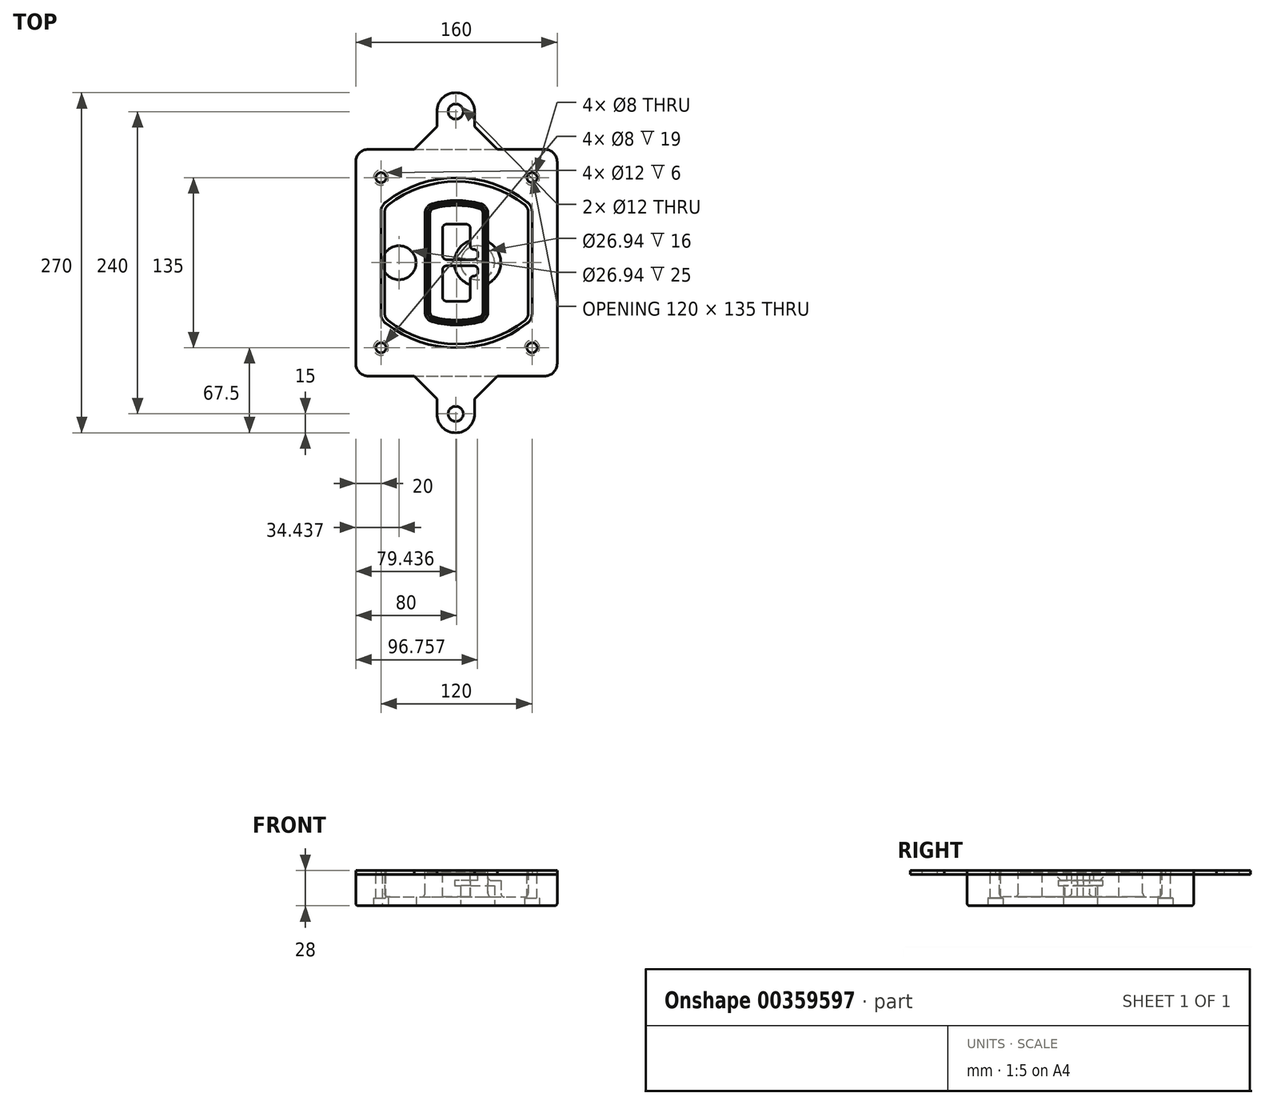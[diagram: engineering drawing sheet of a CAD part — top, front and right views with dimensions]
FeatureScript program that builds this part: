
annotation { "Feature Type Name" : "Feature", "Feature Type Description" : "" }
export const myFeature = defineFeature(function(context is Context, id is Id, definition is map)
    precondition{}
    {
        {
            var Q0;
            Q0=qCreatedBy(makeId("Top.planeOp"),FACE);
            var sketch = newSketch(context, id + "F0", { "sketchPlane" : qUnion([Q0])});
            skPoint(sketch, "E0.rect.middle", {"position": v(0, 0) * mm});
            skLineSegment(sketch, "E1.bottom", {"start": v(-70, -90) * mm, "end": v(70, -90) * mm});
            skLineSegment(sketch, "E1.top", {"start": v(-70, 90) * mm, "end": v(70, 90) * mm});
            skLineSegment(sketch, "E1.left", {"start": v(-80, -80) * mm, "end": v(-80, 80) * mm});
            skLineSegment(sketch, "E1.right", {"start": v(80, -80) * mm, "end": v(80, 80) * mm});
            skLineSegment(sketch, "E2", {"start": v(-80, 90) * mm, "end": v(80, -90) * mm, "construction": true});
            skLineSegment(sketch, "E3", {"start": v(80, 90) * mm, "end": v(-80, -90) * mm, "construction": true});
            skCircle(sketch, "E4", {"center": v(-60, 67.5) * mm, "radius": 4 * mm});
            skCircle(sketch, "E5", {"center": v(60, 67.5) * mm, "radius": 4 * mm});
            skCircle(sketch, "E6", {"center": v(60, -67.5) * mm, "radius": 4 * mm});
            skCircle(sketch, "E7", {"center": v(-60, -67.5) * mm, "radius": 4 * mm});
            skLineSegment(sketch, "E8", {"start": v(-60, 67.5) * mm, "end": v(60, 67.5) * mm, "construction": true});
            skLineSegment(sketch, "E9", {"start": v(60, 67.5) * mm, "end": v(60, -67.5) * mm, "construction": true});
            skLineSegment(sketch, "E10", {"start": v(60, -67.5) * mm, "end": v(-60, -67.5) * mm, "construction": true});
            skLineSegment(sketch, "E11", {"start": v(-60, -67.5) * mm, "end": v(-60, 67.5) * mm, "construction": true});
            skLineSegment(sketch, "E12", {"start": v(-60, 40.3) * mm, "end": v(-60, -40.3) * mm});
            skLineSegment(sketch, "E13", {"start": v(60, 40.3) * mm, "end": v(60, -40.3) * mm});
            skArc(sketch, "E14", {"start": v(56.15, 48.18) * mm, "mid": v(0, 67.5) * mm, "end": v(-56.15, 48.18) * mm});
            skArc(sketch, "E15", {"start": v(-56.15, -48.18) * mm, "mid": v(0, -67.5) * mm, "end": v(56.15, -48.18) * mm});
            skLineSegment(sketch, "E16", {"start": v(-60, 0) * mm, "end": v(60, 0) * mm, "construction": true});
            skPoint(sketch, "E17.visualSharp", {"position": v(-60, -45) * mm});
            skArc(sketch, "E17.filletArc", {"start": v(-60, -40.3) * mm, "mid": v(-58.99, -44.68) * mm, "end": v(-56.15, -48.18) * mm});
            skPoint(sketch, "E18.visualSharp", {"position": v(-60, 45) * mm});
            skArc(sketch, "E18.filletArc", {"start": v(-56.15, 48.18) * mm, "mid": v(-58.99, 44.68) * mm, "end": v(-60, 40.3) * mm});
            skPoint(sketch, "E19.visualSharp", {"position": v(60, 45) * mm});
            skArc(sketch, "E19.filletArc", {"start": v(60, 40.3) * mm, "mid": v(58.99, 44.68) * mm, "end": v(56.15, 48.18) * mm});
            skPoint(sketch, "E20.visualSharp", {"position": v(60, -45) * mm});
            skArc(sketch, "E20.filletArc", {"start": v(56.15, -48.18) * mm, "mid": v(58.99, -44.68) * mm, "end": v(60, -40.3) * mm});
            skPoint(sketch, "E21.visualSharp", {"position": v(-80, 90) * mm});
            skArc(sketch, "E21.filletArc", {"start": v(-70, 90) * mm, "mid": v(-77.07, 87.07) * mm, "end": v(-80, 80) * mm});
            skPoint(sketch, "E22.visualSharp", {"position": v(80, 90) * mm});
            skArc(sketch, "E22.filletArc", {"start": v(80, 80) * mm, "mid": v(77.07, 87.07) * mm, "end": v(70, 90) * mm});
            skPoint(sketch, "E23.visualSharp", {"position": v(80, -90) * mm});
            skArc(sketch, "E23.filletArc", {"start": v(70, -90) * mm, "mid": v(77.07, -87.07) * mm, "end": v(80, -80) * mm});
            skPoint(sketch, "E24.visualSharp", {"position": v(-80, -90) * mm});
            skArc(sketch, "E24.filletArc", {"start": v(-80, -80) * mm, "mid": v(-77.07, -87.07) * mm, "end": v(-70, -90) * mm});
            skArc(sketch, "E25.0", {"start": v(57, 40.3) * mm, "mid": v(56.3, 43.36) * mm, "end": v(54.3, 45.81) * mm});
            skLineSegment(sketch, "E25.1", {"start": v(57, 40.3) * mm, "end": v(57, -40.3) * mm});
            skArc(sketch, "E25.2", {"start": v(54.3, -45.81) * mm, "mid": v(56.3, -43.36) * mm, "end": v(57, -40.3) * mm});
            skArc(sketch, "E25.3", {"start": v(-54.3, -45.81) * mm, "mid": v(0, -64.5) * mm, "end": v(54.3, -45.81) * mm});
            skArc(sketch, "E25.4", {"start": v(-57, -40.3) * mm, "mid": v(-56.3, -43.36) * mm, "end": v(-54.3, -45.81) * mm});
            skArc(sketch, "E25.5", {"start": v(54.3, 45.81) * mm, "mid": v(0, 64.5) * mm, "end": v(-54.3, 45.81) * mm});
            skLineSegment(sketch, "E25.6", {"start": v(-57, 40.3) * mm, "end": v(-57, -40.3) * mm});
            skArc(sketch, "E25.7", {"start": v(-54.3, 45.81) * mm, "mid": v(-56.3, 43.36) * mm, "end": v(-57, 40.3) * mm});
            skArc(sketch, "E26.0", {"start": v(-58.62, 51.33) * mm, "mid": v(-62.58, 46.43) * mm, "end": v(-64, 40.3) * mm});
            skArc(sketch, "E26.1", {"start": v(58.62, 51.33) * mm, "mid": v(0, 71.5) * mm, "end": v(-58.62, 51.33) * mm});
            skArc(sketch, "E26.2", {"start": v(64, 40.3) * mm, "mid": v(62.58, 46.43) * mm, "end": v(58.62, 51.33) * mm});
            skLineSegment(sketch, "E26.3", {"start": v(64, 40.3) * mm, "end": v(64, -40.3) * mm});
            skArc(sketch, "E26.4", {"start": v(58.62, -51.33) * mm, "mid": v(62.58, -46.43) * mm, "end": v(64, -40.3) * mm});
            skLineSegment(sketch, "E26.5", {"start": v(-64, 40.3) * mm, "end": v(-64, -40.3) * mm});
            skArc(sketch, "E26.6", {"start": v(-58.62, -51.33) * mm, "mid": v(0, -71.5) * mm, "end": v(58.62, -51.33) * mm});
            skArc(sketch, "E26.7", {"start": v(-64, -40.3) * mm, "mid": v(-62.58, -46.43) * mm, "end": v(-58.62, -51.33) * mm});
            skSolve(sketch);
        }
        {
            var Q0;
            Q0=makeQuery(id+"F0.imprint","IMPRINT",FACE,{"disambiguationData":[TD([[makeQuery(id+"F0.imprint","IMPRINT",EDGE,{"derivedFrom":sQuery(id+"F0.wireOp",EDGE,"E1.bottom")}),1.0]])]});
            var Q1;
            Q1=makeQuery(id+"F0.imprint","IMPRINT",FACE,{"disambiguationData":[TD([[makeQuery(id+"F0.imprint","IMPRINT",EDGE,{"derivedFrom":sQuery(id+"F0.wireOp",EDGE,"E12")}),1.0]])]});
            var Q2;
            Q2=makeQuery(id+"F0.imprint","IMPRINT",FACE,{"disambiguationData":[TD([[makeQuery(id+"F0.imprint","IMPRINT",EDGE,{"derivedFrom":sQuery(id+"F0.wireOp",EDGE,"E25.0")}),1.0]])]});
            var Q3;
            Q3=makeQuery(id+"F0.imprint","IMPRINT",FACE,{"disambiguationData":[TD([[makeQuery(id+"F0.imprint","IMPRINT",EDGE,{"derivedFrom":sQuery(id+"F0.wireOp",EDGE,"E12")}),-1.0]])]});
            extrude(context, id + "F1", {"entities" : qUnion([Q0, Q1, Q2, Q3]), "oppositeDirection" : true, "depth" : 25 * mm});
        }
        {
            var Q0;
            Q0=makeQuery(id+"F0.imprint","IMPRINT",FACE,{"disambiguationData":[TD([[makeQuery(id+"F0.imprint","IMPRINT",EDGE,{"derivedFrom":sQuery(id+"F0.wireOp",EDGE,"E12")}),1.0]])]});
            extrude(context, id + "F2", {"entities" : qUnion([Q0]), "operationType" : NewBodyOperationType.ADD, "depth" : 3 * mm});
        }
        {
            var Q0;
            Q0=makeQuery(id+"F0.imprint","IMPRINT",FACE,{"disambiguationData":[TD([[makeQuery(id+"F0.imprint","IMPRINT",EDGE,{"derivedFrom":sQuery(id+"F0.wireOp",EDGE,"E25.0")}),1.0]])]});
            extrude(context, id + "F3", {"entities" : qUnion([Q0]), "operationType" : NewBodyOperationType.REMOVE, "oppositeDirection" : true, "depth" : 18 * mm});
        }
        {
            var Q0;
            Q0=makeQuery(id+"F2.opExtrude","CAP_FACE",FACE,{"disambiguationData":[OSD([sQuery(id+"F0.wireOp",EDGE,"E12"),sQuery(id+"F0.wireOp",EDGE,"E13"),sQuery(id+"F0.wireOp",EDGE,"E14"),sQuery(id+"F0.wireOp",EDGE,"E15"),sQuery(id+"F0.wireOp",EDGE,"E17.filletArc"),sQuery(id+"F0.wireOp",EDGE,"E18.filletArc"),sQuery(id+"F0.wireOp",EDGE,"E19.filletArc"),sQuery(id+"F0.wireOp",EDGE,"E20.filletArc"),sQuery(id+"F0.wireOp",EDGE,"E25.0"),sQuery(id+"F0.wireOp",EDGE,"E25.1"),sQuery(id+"F0.wireOp",EDGE,"E25.2"),sQuery(id+"F0.wireOp",EDGE,"E25.3"),sQuery(id+"F0.wireOp",EDGE,"E25.4"),sQuery(id+"F0.wireOp",EDGE,"E25.5"),sQuery(id+"F0.wireOp",EDGE,"E25.6"),sQuery(id+"F0.wireOp",EDGE,"E25.7")])],"isStart":false});
            var sketch = newSketch(context, id + "F4", { "sketchPlane" : qUnion([Q0])});
            skArc(sketch, "E27.0", {"start": v(-19.08, -46.97) * mm, "mid": v(0, -49.5) * mm, "end": v(19.08, -46.97) * mm});
            skArc(sketch, "E28.0", {"start": v(19.08, 46.97) * mm, "mid": v(0, 49.5) * mm, "end": v(-19.08, 46.97) * mm});
            skLineSegment(sketch, "E29", {"start": v(-25, 39.25) * mm, "end": v(-25, -39.25) * mm});
            skLineSegment(sketch, "E30", {"start": v(25, 39.25) * mm, "end": v(25, -39.25) * mm});
            skLineSegment(sketch, "E31", {"start": v(-25, 45.1) * mm, "end": v(25, 45.1) * mm, "construction": true});
            skLineSegment(sketch, "E32", {"start": v(-25, -45.1) * mm, "end": v(25, -45.1) * mm, "construction": true});
            skPoint(sketch, "E33.visualSharp", {"position": v(-25, 45.1) * mm});
            skArc(sketch, "E33.filletArc", {"start": v(-19.08, 46.97) * mm, "mid": v(-23.35, 44.11) * mm, "end": v(-25, 39.25) * mm});
            skPoint(sketch, "E34.visualSharp", {"position": v(25, 45.1) * mm});
            skArc(sketch, "E34.filletArc", {"start": v(25, 39.25) * mm, "mid": v(23.35, 44.11) * mm, "end": v(19.08, 46.97) * mm});
            skPoint(sketch, "E35.visualSharp", {"position": v(25, -45.1) * mm});
            skArc(sketch, "E35.filletArc", {"start": v(19.08, -46.97) * mm, "mid": v(23.35, -44.11) * mm, "end": v(25, -39.25) * mm});
            skPoint(sketch, "E36.visualSharp", {"position": v(-25, -45.1) * mm});
            skArc(sketch, "E36.filletArc", {"start": v(-25, -39.25) * mm, "mid": v(-23.35, -44.11) * mm, "end": v(-19.08, -46.97) * mm});
            skArc(sketch, "E37.0", {"start": v(54.3, 45.81) * mm, "mid": v(0, 64.5) * mm, "end": v(-54.3, 45.81) * mm});
            skArc(sketch, "E37.1", {"start": v(-54.3, 45.81) * mm, "mid": v(-56.3, 43.36) * mm, "end": v(-57, 40.3) * mm});
            skLineSegment(sketch, "E37.2", {"start": v(-57, 40.3) * mm, "end": v(-57, -40.3) * mm});
            skArc(sketch, "E37.3", {"start": v(-57, -40.3) * mm, "mid": v(-56.3, -43.36) * mm, "end": v(-54.3, -45.81) * mm});
            skArc(sketch, "E37.4", {"start": v(-54.3, -45.81) * mm, "mid": v(0, -64.5) * mm, "end": v(54.3, -45.81) * mm});
            skArc(sketch, "E37.5", {"start": v(54.3, -45.81) * mm, "mid": v(56.3, -43.36) * mm, "end": v(57, -40.3) * mm});
            skLineSegment(sketch, "E37.6", {"start": v(57, 40.3) * mm, "end": v(57, -40.3) * mm});
            skArc(sketch, "E37.7", {"start": v(57, 40.3) * mm, "mid": v(56.3, 43.36) * mm, "end": v(54.3, 45.81) * mm});
            skLineSegment(sketch, "E38.0", {"start": v(23, 39.25) * mm, "end": v(23, -39.25) * mm});
            skArc(sketch, "E38.1", {"start": v(18.56, -45.04) * mm, "mid": v(21.76, -42.9) * mm, "end": v(23, -39.25) * mm});
            skArc(sketch, "E38.2", {"start": v(-18.56, -45.04) * mm, "mid": v(0, -47.5) * mm, "end": v(18.56, -45.04) * mm});
            skArc(sketch, "E38.3", {"start": v(-23, -39.25) * mm, "mid": v(-21.76, -42.9) * mm, "end": v(-18.56, -45.04) * mm});
            skLineSegment(sketch, "E38.4", {"start": v(-23, 39.25) * mm, "end": v(-23, -39.25) * mm});
            skArc(sketch, "E38.5", {"start": v(23, 39.25) * mm, "mid": v(21.76, 42.9) * mm, "end": v(18.56, 45.04) * mm});
            skArc(sketch, "E38.6", {"start": v(-18.56, 45.04) * mm, "mid": v(-21.76, 42.9) * mm, "end": v(-23, 39.25) * mm});
            skArc(sketch, "E38.7", {"start": v(18.56, 45.04) * mm, "mid": v(0, 47.5) * mm, "end": v(-18.56, 45.04) * mm});
            skArc(sketch, "E39.0", {"start": v(21, 39.25) * mm, "mid": v(20.18, 41.68) * mm, "end": v(18.04, 43.1) * mm});
            skLineSegment(sketch, "E39.1", {"start": v(21, 39.25) * mm, "end": v(21, -39.25) * mm});
            skArc(sketch, "E39.2", {"start": v(18.04, -43.1) * mm, "mid": v(20.18, -41.68) * mm, "end": v(21, -39.25) * mm});
            skArc(sketch, "E39.3", {"start": v(-18.04, -43.1) * mm, "mid": v(0, -45.5) * mm, "end": v(18.04, -43.1) * mm});
            skArc(sketch, "E39.4", {"start": v(-21, -39.25) * mm, "mid": v(-20.18, -41.68) * mm, "end": v(-18.04, -43.1) * mm});
            skArc(sketch, "E39.5", {"start": v(18.04, 43.1) * mm, "mid": v(0, 45.5) * mm, "end": v(-18.04, 43.1) * mm});
            skLineSegment(sketch, "E39.6", {"start": v(-21, 39.25) * mm, "end": v(-21, -39.25) * mm});
            skArc(sketch, "E39.7", {"start": v(-18.04, 43.1) * mm, "mid": v(-20.18, 41.68) * mm, "end": v(-21, 39.25) * mm});
            skLineSegment(sketch, "E40", {"start": v(-25, 0) * mm, "end": v(25, 0) * mm, "construction": true});
            skLineSegment(sketch, "E41", {"start": v(-11, 5.5) * mm, "end": v(-11, 27.5) * mm});
            skLineSegment(sketch, "E42", {"start": v(-8, 30.5) * mm, "end": v(8, 30.5) * mm});
            skLineSegment(sketch, "E43", {"start": v(11, 27.5) * mm, "end": v(11, 13.5) * mm});
            skLineSegment(sketch, "E44", {"start": v(14, 10.5) * mm, "end": v(14, 10.5) * mm});
            skLineSegment(sketch, "E45", {"start": v(17, 7.5) * mm, "end": v(17, 5.5) * mm});
            skLineSegment(sketch, "E46", {"start": v(14, 2.5) * mm, "end": v(-8, 2.5) * mm});
            skPoint(sketch, "E47.visualSharp", {"position": v(-11, 30.5) * mm});
            skArc(sketch, "E47.filletArc", {"start": v(-8, 30.5) * mm, "mid": v(-10.12, 29.62) * mm, "end": v(-11, 27.5) * mm});
            skPoint(sketch, "E48.visualSharp", {"position": v(11, 30.5) * mm});
            skArc(sketch, "E48.filletArc", {"start": v(11, 27.5) * mm, "mid": v(10.12, 29.62) * mm, "end": v(8, 30.5) * mm});
            skPoint(sketch, "E49.visualSharp", {"position": v(11, 10.5) * mm});
            skArc(sketch, "E49.filletArc", {"start": v(11, 13.5) * mm, "mid": v(11.88, 11.38) * mm, "end": v(14, 10.5) * mm});
            skPoint(sketch, "E50.visualSharp", {"position": v(17, 10.5) * mm});
            skArc(sketch, "E50.filletArc", {"start": v(17, 7.5) * mm, "mid": v(16.12, 9.62) * mm, "end": v(14, 10.5) * mm});
            skPoint(sketch, "E51.visualSharp", {"position": v(17, 2.5) * mm});
            skArc(sketch, "E51.filletArc", {"start": v(14, 2.5) * mm, "mid": v(16.12, 3.38) * mm, "end": v(17, 5.5) * mm});
            skPoint(sketch, "E52.visualSharp", {"position": v(-11, 2.5) * mm});
            skArc(sketch, "E52.filletArc", {"start": v(-11, 5.5) * mm, "mid": v(-10.12, 3.38) * mm, "end": v(-8, 2.5) * mm});
            skLineSegment(sketch, "E53.0.MirrorCS", {"start": v(14, -2.5) * mm, "end": v(-8, -2.5) * mm});
            skArc(sketch, "E54.0.MirrorCS", {"start": v(-11, -5.5) * mm, "mid": v(-10.12, -3.38) * mm, "end": v(-8, -2.5) * mm});
            skLineSegment(sketch, "E55.0.MirrorCS", {"start": v(-11, -5.5) * mm, "end": v(-11, -27.5) * mm});
            skArc(sketch, "E56.0.MirrorCS", {"start": v(-8, -30.5) * mm, "mid": v(-10.12, -29.62) * mm, "end": v(-11, -27.5) * mm});
            skLineSegment(sketch, "E57.0.MirrorCS", {"start": v(-8, -30.5) * mm, "end": v(8, -30.5) * mm});
            skArc(sketch, "E58.0.MirrorCS", {"start": v(11, -27.5) * mm, "mid": v(10.12, -29.62) * mm, "end": v(8, -30.5) * mm});
            skLineSegment(sketch, "E59.0.MirrorCS", {"start": v(11, -27.5) * mm, "end": v(11, -13.5) * mm});
            skArc(sketch, "E60.0.MirrorCS", {"start": v(11, -13.5) * mm, "mid": v(11.88, -11.38) * mm, "end": v(14, -10.5) * mm});
            skArc(sketch, "E61.0.MirrorCS", {"start": v(17, -7.5) * mm, "mid": v(16.12, -9.62) * mm, "end": v(14, -10.5) * mm});
            skLineSegment(sketch, "E62.0.MirrorCS", {"start": v(17, -7.5) * mm, "end": v(17, -5.5) * mm});
            skArc(sketch, "E63.0.MirrorCS", {"start": v(14, -2.5) * mm, "mid": v(16.12, -3.38) * mm, "end": v(17, -5.5) * mm});
            skSolve(sketch);
        }
        {
            var Q0;
            Q0=makeQuery(id+"F4.imprint","IMPRINT",FACE,{"disambiguationData":[TD([[makeQuery(id+"F4.imprint","IMPRINT",EDGE,{"derivedFrom":sQuery(id+"F4.wireOp",EDGE,"E27.0")}),1.0]])]});
            var Q1;
            Q1=makeQuery(id+"F4.imprint","IMPRINT",FACE,{"disambiguationData":[TD([[makeQuery(id+"F4.imprint","IMPRINT",EDGE,{"derivedFrom":sQuery(id+"F4.wireOp",EDGE,"E38.0")}),-1.0]])]});
            var Q2;
            Q2=makeQuery(id+"F4.imprint","IMPRINT",FACE,{"disambiguationData":[TD([[makeQuery(id+"F4.imprint","IMPRINT",EDGE,{"derivedFrom":sQuery(id+"F4.wireOp",EDGE,"E39.0")}),1.0]])]});
            extrude(context, id + "F5", {"entities" : qUnion([Q0, Q1, Q2]), "operationType" : NewBodyOperationType.ADD, "endBound" : BoundingType.UP_TO_NEXT, "oppositeDirection" : true, "depth" : 25 * mm});
        }
        {
            var Q0;
            Q0=makeQuery(id+"F4.imprint","IMPRINT",FACE,{"disambiguationData":[TD([[makeQuery(id+"F4.imprint","IMPRINT",EDGE,{"derivedFrom":sQuery(id+"F4.wireOp",EDGE,"E38.0")}),-1.0]])]});
            extrude(context, id + "F6", {"entities" : qUnion([Q0]), "operationType" : NewBodyOperationType.REMOVE, "oppositeDirection" : true, "depth" : 2 * mm});
        }
        {
            var Q0;
            Q0=makeQuery(id+"F1.opExtrude","CAP_FACE",FACE,{"disambiguationData":[OSD([sQuery(id+"F0.wireOp",EDGE,"E1.bottom"),sQuery(id+"F0.wireOp",EDGE,"E1.top"),sQuery(id+"F0.wireOp",EDGE,"E1.left"),sQuery(id+"F0.wireOp",EDGE,"E1.right"),sQuery(id+"F0.wireOp",EDGE,"E4"),sQuery(id+"F0.wireOp",EDGE,"E5"),sQuery(id+"F0.wireOp",EDGE,"E6"),sQuery(id+"F0.wireOp",EDGE,"E7"),sQuery(id+"F0.wireOp",EDGE,"E21.filletArc"),sQuery(id+"F0.wireOp",EDGE,"E22.filletArc"),sQuery(id+"F0.wireOp",EDGE,"E23.filletArc"),sQuery(id+"F0.wireOp",EDGE,"E24.filletArc")])],"isStart":false});
            var sketch = newSketch(context, id + "F7", { "sketchPlane" : qUnion([Q0])});
            skCircle(sketch, "E64", {"center": v(16.76, 0) * mm, "radius": 13.47 * mm});
            skCircle(sketch, "E65", {"center": v(-45.56, 0) * mm, "radius": 13.47 * mm});
            skLineSegment(sketch, "E66", {"start": v(80, 0) * mm, "end": v(-80, 0) * mm});
            skCircle(sketch, "E67", {"center": v(16.76, 0) * mm, "radius": 18.47 * mm});
            skCircle(sketch, "E68", {"center": v(60, -67.5) * mm, "radius": 6 * mm});
            skCircle(sketch, "E69", {"center": v(-60, -67.5) * mm, "radius": 6 * mm});
            skCircle(sketch, "E70", {"center": v(-60, 67.5) * mm, "radius": 6 * mm});
            skCircle(sketch, "E71", {"center": v(60, 67.5) * mm, "radius": 6 * mm});
            skSolve(sketch);
        }
        {
            var Q0;
            {var subQ1=sQuery(id+"F7.wireOp",EDGE,"E66");var subQ4=sQuery(id+"F7.wireOp",EDGE,"E64");var subQ6=makeQuery(id+"F7.imprint","INTERSECT",VERTEX,{"disambiguationData":[OD(0.0)],"derivedFrom":[subQ4,subQ1]});Q0=makeQuery(id+"F7.imprint","IMPRINT",FACE,{"disambiguationData":[TD([[makeQuery(id+"F7.imprint","IMPRINT",EDGE,{"disambiguationData":[TD([[subQ6,-1.0]])],"derivedFrom":subQ4}),-1.0]])]});}
            var Q1;
            {var subQ0=sQuery(id+"F7.wireOp",EDGE,"E66");var subQ1=sQuery(id+"F7.wireOp",EDGE,"E64");var subQ3=makeQuery(id+"F7.imprint","INTERSECT",VERTEX,{"disambiguationData":[OD(0.0)],"derivedFrom":[subQ1,subQ0]});Q1=makeQuery(id+"F7.imprint","IMPRINT",FACE,{"disambiguationData":[TD([[makeQuery(id+"F7.imprint","IMPRINT",EDGE,{"disambiguationData":[TD([[subQ3,-1.0]])],"derivedFrom":subQ1}),1.0]])]});}
            var Q2;
            {var subQ0=sQuery(id+"F7.wireOp",EDGE,"E66");var subQ1=sQuery(id+"F7.wireOp",EDGE,"E64");var subQ3=makeQuery(id+"F7.imprint","INTERSECT",VERTEX,{"disambiguationData":[OD(0.0)],"derivedFrom":[subQ1,subQ0]});Q2=makeQuery(id+"F7.imprint","IMPRINT",FACE,{"disambiguationData":[TD([[makeQuery(id+"F7.imprint","IMPRINT",EDGE,{"disambiguationData":[TD([[subQ3,1.0]])],"derivedFrom":subQ1}),1.0]])]});}
            var Q3;
            {var subQ1=sQuery(id+"F7.wireOp",EDGE,"E66");var subQ4=sQuery(id+"F7.wireOp",EDGE,"E64");var subQ6=makeQuery(id+"F7.imprint","INTERSECT",VERTEX,{"disambiguationData":[OD(0.0)],"derivedFrom":[subQ4,subQ1]});Q3=makeQuery(id+"F7.imprint","IMPRINT",FACE,{"disambiguationData":[TD([[makeQuery(id+"F7.imprint","IMPRINT",EDGE,{"disambiguationData":[TD([[subQ6,1.0]])],"derivedFrom":subQ4}),-1.0]])]});}
            extrude(context, id + "F8", {"entities" : qUnion([Q0, Q1, Q2, Q3]), "operationType" : NewBodyOperationType.ADD, "oppositeDirection" : true, "depth" : 20 * mm});
        }
        {
            var Q0;
            {var subQ0=sQuery(id+"F7.wireOp",EDGE,"E66");var subQ1=sQuery(id+"F7.wireOp",EDGE,"E64");var subQ3=makeQuery(id+"F7.imprint","INTERSECT",VERTEX,{"disambiguationData":[OD(0.0)],"derivedFrom":[subQ1,subQ0]});Q0=makeQuery(id+"F7.imprint","IMPRINT",FACE,{"disambiguationData":[TD([[makeQuery(id+"F7.imprint","IMPRINT",EDGE,{"disambiguationData":[TD([[subQ3,-1.0]])],"derivedFrom":subQ1}),1.0]])]});}
            var Q1;
            {var subQ0=sQuery(id+"F7.wireOp",EDGE,"E66");var subQ1=sQuery(id+"F7.wireOp",EDGE,"E64");var subQ3=makeQuery(id+"F7.imprint","INTERSECT",VERTEX,{"disambiguationData":[OD(0.0)],"derivedFrom":[subQ1,subQ0]});Q1=makeQuery(id+"F7.imprint","IMPRINT",FACE,{"disambiguationData":[TD([[makeQuery(id+"F7.imprint","IMPRINT",EDGE,{"disambiguationData":[TD([[subQ3,1.0]])],"derivedFrom":subQ1}),1.0]])]});}
            extrude(context, id + "F9", {"entities" : qUnion([Q0, Q1]), "operationType" : NewBodyOperationType.REMOVE, "oppositeDirection" : true, "depth" : 16 * mm});
        }
        {
            var Q0;
            {var subQ0=sQuery(id+"F7.wireOp",EDGE,"E66");var subQ1=sQuery(id+"F7.wireOp",EDGE,"E65");var subQ3=makeQuery(id+"F7.imprint","INTERSECT",VERTEX,{"disambiguationData":[OD(0.0)],"derivedFrom":[subQ1,subQ0]});Q0=makeQuery(id+"F7.imprint","IMPRINT",FACE,{"disambiguationData":[TD([[makeQuery(id+"F7.imprint","IMPRINT",EDGE,{"disambiguationData":[TD([[subQ3,-1.0]])],"derivedFrom":subQ1}),1.0]])]});}
            var Q1;
            {var subQ0=sQuery(id+"F7.wireOp",EDGE,"E66");var subQ1=sQuery(id+"F7.wireOp",EDGE,"E65");var subQ3=makeQuery(id+"F7.imprint","INTERSECT",VERTEX,{"disambiguationData":[OD(0.0)],"derivedFrom":[subQ1,subQ0]});Q1=makeQuery(id+"F7.imprint","IMPRINT",FACE,{"disambiguationData":[TD([[makeQuery(id+"F7.imprint","IMPRINT",EDGE,{"disambiguationData":[TD([[subQ3,1.0]])],"derivedFrom":subQ1}),1.0]])]});}
            extrude(context, id + "F10", {"entities" : qUnion([Q0, Q1]), "operationType" : NewBodyOperationType.REMOVE, "oppositeDirection" : true, "depth" : 25 * mm});
        }
        {
            var Q0;
            Q0=makeQuery(id+"F7.imprint","IMPRINT",FACE,{"disambiguationData":[TD([[makeQuery(id+"F7.imprint","IMPRINT",EDGE,{"derivedFrom":sQuery(id+"F7.wireOp",EDGE,"E68")}),1.0]])]});
            var Q1;
            Q1=makeQuery(id+"F7.imprint","IMPRINT",FACE,{"disambiguationData":[TD([[makeQuery(id+"F7.imprint","IMPRINT",EDGE,{"derivedFrom":makeQuery(id+"F1.opExtrude","CAP_EDGE",EDGE,{"disambiguationData":[OSD([sQuery(id+"F0.wireOp",EDGE,"E5")])],"isStart":false})}),-1.0]])]});
            var Q2;
            Q2=makeQuery(id+"F7.imprint","IMPRINT",FACE,{"disambiguationData":[TD([[makeQuery(id+"F7.imprint","IMPRINT",EDGE,{"derivedFrom":sQuery(id+"F7.wireOp",EDGE,"E69")}),1.0]])]});
            var Q3;
            Q3=makeQuery(id+"F7.imprint","IMPRINT",FACE,{"disambiguationData":[TD([[makeQuery(id+"F7.imprint","IMPRINT",EDGE,{"derivedFrom":makeQuery(id+"F1.opExtrude","CAP_EDGE",EDGE,{"disambiguationData":[OSD([sQuery(id+"F0.wireOp",EDGE,"E4")])],"isStart":false})}),-1.0]])]});
            var Q4;
            Q4=makeQuery(id+"F7.imprint","IMPRINT",FACE,{"disambiguationData":[TD([[makeQuery(id+"F7.imprint","IMPRINT",EDGE,{"derivedFrom":sQuery(id+"F7.wireOp",EDGE,"E70")}),1.0]])]});
            var Q5;
            Q5=makeQuery(id+"F7.imprint","IMPRINT",FACE,{"disambiguationData":[TD([[makeQuery(id+"F7.imprint","IMPRINT",EDGE,{"derivedFrom":makeQuery(id+"F1.opExtrude","CAP_EDGE",EDGE,{"disambiguationData":[OSD([sQuery(id+"F0.wireOp",EDGE,"E7")])],"isStart":false})}),-1.0]])]});
            var Q6;
            Q6=makeQuery(id+"F7.imprint","IMPRINT",FACE,{"disambiguationData":[TD([[makeQuery(id+"F7.imprint","IMPRINT",EDGE,{"derivedFrom":sQuery(id+"F7.wireOp",EDGE,"E71")}),1.0]])]});
            var Q7;
            Q7=makeQuery(id+"F7.imprint","IMPRINT",FACE,{"disambiguationData":[TD([[makeQuery(id+"F7.imprint","IMPRINT",EDGE,{"derivedFrom":makeQuery(id+"F1.opExtrude","CAP_EDGE",EDGE,{"disambiguationData":[OSD([sQuery(id+"F0.wireOp",EDGE,"E6")])],"isStart":false})}),-1.0]])]});
            extrude(context, id + "F11", {"entities" : qUnion([Q0, Q1, Q2, Q3, Q4, Q5, Q6, Q7]), "operationType" : NewBodyOperationType.REMOVE, "oppositeDirection" : true, "depth" : 6 * mm});
        }
        {
            var Q0;
            Q0=makeQuery(id+"F9.boolean.opBoolean","COPY",FACE,{"derivedFrom":makeQuery(id+"F9.opExtrude","CAP_FACE",FACE,{"disambiguationData":[OSD([sQuery(id+"F7.wireOp",EDGE,"E64")])],"isStart":false})});
            var sketch = newSketch(context, id + "F12", { "sketchPlane" : qUnion([Q0])});
            skArc(sketch, "E72.0", {"start": v(11, 17.55) * mm, "mid": v(2.57, 11.82) * mm, "end": v(-1.54, 2.5) * mm});
            skArc(sketch, "E72.1", {"start": v(-1.54, -2.5) * mm, "mid": v(2.57, -11.82) * mm, "end": v(11, -17.55) * mm});
            skLineSegment(sketch, "E73", {"start": v(-1.54, -2.5) * mm, "end": v(14, -2.5) * mm});
            skLineSegment(sketch, "E74.0", {"start": v(14, 2.5) * mm, "end": v(-1.54, 2.5) * mm});
            skArc(sketch, "E74.1", {"start": v(14, 2.5) * mm, "mid": v(16.12, 3.38) * mm, "end": v(17, 5.5) * mm});
            skLineSegment(sketch, "E74.2", {"start": v(17, 7.5) * mm, "end": v(17, 5.5) * mm});
            skArc(sketch, "E74.3", {"start": v(17, 7.5) * mm, "mid": v(16.12, 9.62) * mm, "end": v(14, 10.5) * mm});
            skArc(sketch, "E74.4", {"start": v(11, 13.5) * mm, "mid": v(11.88, 11.38) * mm, "end": v(14, 10.5) * mm});
            skLineSegment(sketch, "E74.5", {"start": v(11, 17.55) * mm, "end": v(11, 13.5) * mm});
            skLineSegment(sketch, "E74.7", {"start": v(14, -2.5) * mm, "end": v(-1.54, -2.5) * mm});
            skArc(sketch, "E74.8", {"start": v(14, -2.5) * mm, "mid": v(16.12, -3.38) * mm, "end": v(17, -5.5) * mm});
            skLineSegment(sketch, "E74.9", {"start": v(17, -7.5) * mm, "end": v(17, -5.5) * mm});
            skArc(sketch, "E74.10", {"start": v(17, -7.5) * mm, "mid": v(16.12, -9.62) * mm, "end": v(14, -10.5) * mm});
            skArc(sketch, "E74.11", {"start": v(11, -13.5) * mm, "mid": v(11.88, -11.38) * mm, "end": v(14, -10.5) * mm});
            skLineSegment(sketch, "E74.12", {"start": v(11, -17.55) * mm, "end": v(11, -13.5) * mm});
            skPoint(sketch, "E75.orphan", {"position": v(11, -27.5) * mm});
            skPoint(sketch, "E76.orphan", {"position": v(-8, -2.5) * mm});
            skPoint(sketch, "E77.orphan", {"position": v(-8, 2.5) * mm});
            skPoint(sketch, "E78.orphan", {"position": v(11, 27.5) * mm});
            skSolve(sketch);
        }
        {
            var Q0;
            {var subQ7=sQuery(id+"F12.wireOp",EDGE,"E72.0");var subQ14=sQuery(id+"F12.wireOp",EDGE,"E72.1");var subQ16=sQuery(id+"F12.wireOp",EDGE,"E74.1");var subQ18=sQuery(id+"F12.wireOp",EDGE,"E74.8");Q0=qUnion([makeQuery(id+"F12.imprint","IMPRINT",FACE,{"disambiguationData":[TD([[makeQuery(id+"F12.imprint","IMPRINT",EDGE,{"derivedFrom":subQ7}),1.0]])]}),makeQuery(id+"F12.imprint","IMPRINT",FACE,{"disambiguationData":[TD([[makeQuery(id+"F12.imprint","IMPRINT",EDGE,{"derivedFrom":subQ14}),1.0]])]}),makeQuery(id+"F12.imprint","IMPRINT",FACE,{"disambiguationData":[TD([[makeQuery(id+"F12.imprint","IMPRINT",EDGE,{"derivedFrom":subQ16}),1.0]])]}),makeQuery(id+"F12.imprint","IMPRINT",FACE,{"disambiguationData":[TD([[makeQuery(id+"F12.imprint","IMPRINT",EDGE,{"derivedFrom":subQ18}),-1.0]])]})]);}
            var Q1;
            Q1=makeQuery(id+"F5.boolean.opBoolean","SPLIT",FACE,{"disambiguationData":[TD([makeQuery(id+"F5.opExtrude","SWEPT_FACE",FACE,{"disambiguationData":[OSD([sQuery(id+"F4.wireOp",EDGE,"E41")])]})])],"derivedFrom":makeQuery(id+"F3.boolean.opBoolean","COPY",FACE,{"derivedFrom":makeQuery(id+"F3.opExtrude","CAP_FACE",FACE,{"disambiguationData":[OSD([sQuery(id+"F0.wireOp",EDGE,"E25.0"),sQuery(id+"F0.wireOp",EDGE,"E25.1"),sQuery(id+"F0.wireOp",EDGE,"E25.2"),sQuery(id+"F0.wireOp",EDGE,"E25.3"),sQuery(id+"F0.wireOp",EDGE,"E25.4"),sQuery(id+"F0.wireOp",EDGE,"E25.5"),sQuery(id+"F0.wireOp",EDGE,"E25.6"),sQuery(id+"F0.wireOp",EDGE,"E25.7")])],"isStart":false})})});
            extrude(context, id + "F13", {"entities" : qUnion([Q0]), "operationType" : NewBodyOperationType.REMOVE, "endBound" : BoundingType.UP_TO_SURFACE, "endBoundEntityFace" : qUnion([Q1]), "depth" : 25 * mm});
        }
        {
            var Q0;
            Q0=makeQuery(id+"F3.boolean.opBoolean","COPY",EDGE,{"derivedFrom":makeQuery(id+"F3.opExtrude","CAP_EDGE",EDGE,{"disambiguationData":[OSD([sQuery(id+"F0.wireOp",EDGE,"E25.6")])],"isStart":false})});
            var Q1;
            Q1=makeQuery(id+"F8.boolean.opBoolean","INTERSECT",EDGE,{"derivedFrom":[makeQuery(id+"F5.opExtrude","SWEPT_FACE",FACE,{"disambiguationData":[OSD([sQuery(id+"F4.wireOp",EDGE,"E30")])]}),makeQuery(id+"F8.opExtrude","CAP_FACE",FACE,{"disambiguationData":[OSD([sQuery(id+"F7.wireOp",EDGE,"E67")])],"isStart":false})]});
            var Q2;
            Q2=makeQuery(id+"F8.boolean.opBoolean","INTERSECT",EDGE,{"disambiguationData":[OD(1.0)],"derivedFrom":[makeQuery(id+"F5.opExtrude","SWEPT_FACE",FACE,{"disambiguationData":[OSD([sQuery(id+"F4.wireOp",EDGE,"E30")])]}),makeQuery(id+"F8.opExtrude","SWEPT_FACE",FACE,{"disambiguationData":[OSD([sQuery(id+"F7.wireOp",EDGE,"E67")])]})]});
            var Q3;
            {var subQ0=sQuery(id+"F4.wireOp",EDGE,"E30");Q3=makeQuery(id+"F8.boolean.opBoolean","SPLIT",EDGE,{"disambiguationData":[TD([makeQuery(id+"F5.opExtrude","SWEPT_FACE",FACE,{"disambiguationData":[OSD([sQuery(id+"F4.wireOp",EDGE,"E35.filletArc")])]})])],"derivedFrom":makeQuery(id+"F5.opExtrude","CAP_EDGE",EDGE,{"disambiguationData":[OSD([subQ0])],"isStart":false})});}
            var Q4;
            {var subQ0=sQuery(id+"F0.wireOp",EDGE,"E25.7");var subQ1=sQuery(id+"F0.wireOp",EDGE,"E25.1");var subQ2=sQuery(id+"F0.wireOp",EDGE,"E25.6");var subQ3=sQuery(id+"F0.wireOp",EDGE,"E25.5");var subQ4=sQuery(id+"F0.wireOp",EDGE,"E25.4");var subQ5=sQuery(id+"F0.wireOp",EDGE,"E25.0");var subQ6=sQuery(id+"F0.wireOp",EDGE,"E25.2");var subQ7=sQuery(id+"F0.wireOp",EDGE,"E25.3");Q4=makeQuery(id+"F8.boolean.opBoolean","INTERSECT",EDGE,{"derivedFrom":[makeQuery(id+"F5.boolean.opBoolean","SPLIT",FACE,{"disambiguationData":[TD([makeQuery(id+"F2.opExtrude","SWEPT_FACE",FACE,{"disambiguationData":[OSD([subQ5])]})])],"derivedFrom":makeQuery(id+"F3.boolean.opBoolean","COPY",FACE,{"derivedFrom":makeQuery(id+"F3.opExtrude","CAP_FACE",FACE,{"disambiguationData":[OSD([subQ5,subQ1,subQ6,subQ7,subQ4,subQ3,subQ2,subQ0])],"isStart":false})})}),makeQuery(id+"F8.opExtrude","SWEPT_FACE",FACE,{"disambiguationData":[OSD([sQuery(id+"F7.wireOp",EDGE,"E67")])]})]});}
            var Q5;
            Q5=makeQuery(id+"F8.boolean.opBoolean","INTERSECT",EDGE,{"disambiguationData":[OD(0.0)],"derivedFrom":[makeQuery(id+"F5.opExtrude","SWEPT_FACE",FACE,{"disambiguationData":[OSD([sQuery(id+"F4.wireOp",EDGE,"E30")])]}),makeQuery(id+"F8.opExtrude","SWEPT_FACE",FACE,{"disambiguationData":[OSD([sQuery(id+"F7.wireOp",EDGE,"E67")])]})]});
            fillet(context, id + "F14", {"entities" : qUnion([Q0, Q1, Q2, Q3, Q4, Q5]), "radius" : 3 * mm, "tangentPropagation" : true, "allowEdgeOverflow" : false});
        }
        {
            var Q0;
            Q0=makeQuery(id+"F1.opExtrude","CAP_EDGE",EDGE,{"disambiguationData":[OSD([sQuery(id+"F0.wireOp",EDGE,"E1.bottom")])],"isStart":false});
            fillet(context, id + "F15", {"entities" : qUnion([Q0]), "radius" : 2 * mm, "tangentPropagation" : true, "allowEdgeOverflow" : false});
        }
        {
            var Q0;
            {var subQ0=sQuery(id+"F0.wireOp",EDGE,"E21.filletArc");var subQ1=sQuery(id+"F0.wireOp",EDGE,"E7");var subQ2=sQuery(id+"F0.wireOp",EDGE,"E6");var subQ3=sQuery(id+"F0.wireOp",EDGE,"E5");var subQ4=sQuery(id+"F0.wireOp",EDGE,"E4");var subQ5=sQuery(id+"F0.wireOp",EDGE,"E22.filletArc");var subQ6=sQuery(id+"F0.wireOp",EDGE,"E1.bottom");var subQ7=sQuery(id+"F0.wireOp",EDGE,"E1.right");var subQ8=sQuery(id+"F0.wireOp",EDGE,"E1.top");var subQ9=sQuery(id+"F0.wireOp",EDGE,"E1.left");var subQ10=sQuery(id+"F0.wireOp",EDGE,"E23.filletArc");var subQ11=sQuery(id+"F0.wireOp",EDGE,"E24.filletArc");Q0=makeQuery(id+"F2.boolean.opBoolean","SPLIT",FACE,{"disambiguationData":[TD([makeQuery(id+"F1.opExtrude","SWEPT_FACE",FACE,{"disambiguationData":[OSD([subQ6])]})])],"derivedFrom":makeQuery(id+"F1.opExtrude","CAP_FACE",FACE,{"disambiguationData":[OSD([subQ6,subQ8,subQ9,subQ7,subQ4,subQ3,subQ2,subQ1,subQ0,subQ5,subQ10,subQ11])],"isStart":true})});}
            var sketch = newSketch(context, id + "F16", { "sketchPlane" : qUnion([Q0])});
            skLineSegment(sketch, "E79", {"start": v(-38.73, 90) * mm, "end": v(51.81, 90) * mm});
            skLineSegment(sketch, "E80", {"start": v(-33.56, 90) * mm, "end": v(-15.56, 108) * mm});
            skLineSegment(sketch, "E81", {"start": v(-15.56, 108) * mm, "end": v(-15.56, 120) * mm});
            skLineSegment(sketch, "E82", {"start": v(32.44, 90) * mm, "end": v(14.44, 108) * mm});
            skLineSegment(sketch, "E83", {"start": v(14.44, 108) * mm, "end": v(14.44, 120) * mm});
            skArc(sketch, "E84", {"start": v(-15.56, 120) * mm, "mid": v(-0.56, 135) * mm, "end": v(14.44, 120) * mm});
            skLineSegment(sketch, "E85", {"start": v(-0.56, 90) * mm, "end": v(-0.56, 120) * mm, "construction": true});
            skCircle(sketch, "E86", {"center": v(-0.56, 120) * mm, "radius": 6 * mm});
            skLineSegment(sketch, "E87", {"start": v(-80, 0) * mm, "end": v(80, 0) * mm, "construction": true});
            skLineSegment(sketch, "E88.MirrorCS", {"start": v(-0.56, -90) * mm, "end": v(-0.56, -120) * mm, "construction": true});
            skArc(sketch, "E89.MirrorCS", {"start": v(-15.56, -120) * mm, "mid": v(-0.56, -135) * mm, "end": v(14.44, -120) * mm});
            skLineSegment(sketch, "E90.MirrorCS", {"start": v(14.44, -108) * mm, "end": v(14.44, -120) * mm});
            skCircle(sketch, "E91.MirrorC", {"center": v(-0.56, -120) * mm, "radius": 6 * mm});
            skLineSegment(sketch, "E92.MirrorCS", {"start": v(32.44, -90) * mm, "end": v(14.44, -108) * mm});
            skLineSegment(sketch, "E93.MirrorCS", {"start": v(-15.56, -108) * mm, "end": v(-15.56, -120) * mm});
            skLineSegment(sketch, "E94.MirrorCS", {"start": v(-33.56, -90) * mm, "end": v(-15.56, -108) * mm});
            skLineSegment(sketch, "E95", {"start": v(-33.56, -90) * mm, "end": v(32.44, -90) * mm});
            skSolve(sketch);
        }
        {
            var Q0;
            Q0 = qSketchRegion(id + "F16", true);
            var Q1;
            {var subQ8=sQuery(id+"F16.wireOp",EDGE,"E95");Q1=makeQuery(id+"F16.imprint","IMPRINT",FACE,{"disambiguationData":[TD([[makeQuery(id+"F16.imprint","IMPRINT",EDGE,{"derivedFrom":subQ8}),1.0]])]});}
            var Q2;
            Q2=makeQuery(id+"F2.opExtrude","CAP_FACE",FACE,{"disambiguationData":[OSD([sQuery(id+"F0.wireOp",EDGE,"E12"),sQuery(id+"F0.wireOp",EDGE,"E13"),sQuery(id+"F0.wireOp",EDGE,"E14"),sQuery(id+"F0.wireOp",EDGE,"E15"),sQuery(id+"F0.wireOp",EDGE,"E17.filletArc"),sQuery(id+"F0.wireOp",EDGE,"E18.filletArc"),sQuery(id+"F0.wireOp",EDGE,"E19.filletArc"),sQuery(id+"F0.wireOp",EDGE,"E20.filletArc"),sQuery(id+"F0.wireOp",EDGE,"E25.0"),sQuery(id+"F0.wireOp",EDGE,"E25.1"),sQuery(id+"F0.wireOp",EDGE,"E25.2"),sQuery(id+"F0.wireOp",EDGE,"E25.3"),sQuery(id+"F0.wireOp",EDGE,"E25.4"),sQuery(id+"F0.wireOp",EDGE,"E25.5"),sQuery(id+"F0.wireOp",EDGE,"E25.6"),sQuery(id+"F0.wireOp",EDGE,"E25.7")])],"isStart":false});
            extrude(context, id + "F17", {"entities" : qUnion([Q0, Q1]), "endBound" : BoundingType.UP_TO_SURFACE, "endBoundEntityFace" : qUnion([Q2]), "depth" : 25 * mm});
        }
    });
